# Revit family: Haworth_AWood_Desk_Rectangular_EU_PRELIMINARY
name_source: partatom
category: Furniture
units: mm (PartAtom-declared; Revit-internal decimal feet)

## family parameters
Always vertical = Yes
Cut with Voids When Loaded = No
OmniClass Number = 23.40.70.14.64.11
OmniClass Title = Office Furniture
Room Calculation Point = No
Shared = No
Work Plane-Based = No

## types (8) — shared parameters
Actual Height = 73 cm
Assembly Code = E2020200
Description = Haworth - A_Wood - Desk - Rectangular
Flip Top Finish = Haworth _ Paint _ Metallic Silver
Leg Height = 70 cm
Manufacturer = Haworth
Model = AWRDXXXX
Revision Number = 1
Size = Verify Final Dim.w/ Haworth
Trim Finish = Haworth _ Metal _ Structured White EC
URL = https://www.haworth.com
URL - Product = https://www.haworth.com
Warranty = http://www.haworth.com
Worksurface 100 Depth = 160x100, 180x100cm
Worksurface 60 Depth = 60x60, 80x60, 100x60, 120x60, 140x60cm
Worksurface 80 Depth = 80x80, 100x80, 120x80, 140x80, 160x80, 180x80cm
Worksurface 90 Depth = 140x90, 160x90, 180x90cm

## per-type parameters (varying)
| type | Accessory Kit | Actual Depth | Actual Width | Flip Top Cable Outlet | No Accessory Kit | Rectangle | Round Cable Outlet | Rounded Corners | Scallop | Squared Corners | Void Depth |
| 60 x 60 | No | 60 cm | 60 cm | No | Yes | Yes | No | No | No | Yes | 0 cm |
| 120 x 80 | Yes | 80 cm | 120 cm | No | No | No | Yes | Yes | Yes | No | 5 cm |
| 180 x 90 | Yes | 90 cm | 180 cm | No | No | No | Yes | Yes | Yes | No | 5 cm |
| 160 x 100 | Yes | 100 cm | 160 cm | No | No | No | No | Yes | Yes | No | 5 cm |
| 180 x 100 | Yes | 100 cm | 180 cm | No | No | No | Yes | No | Yes | Yes | 5 cm |
| 100 x 60 | Yes | 60 cm | 100 cm | Yes | No | Yes | No | No | No | Yes | 0 cm |
| 180 x 80 | No | 80 cm | 180 cm | No | Yes | Yes | No | No | No | Yes | 0 cm |
| 140 x 90 | No | 90 cm | 140 cm | No | Yes | Yes | No | No | No | Yes | 0 cm |

## geometry (parser evidence)
native form markers: Sweep x12
no freeform markers — native parametric forms only
